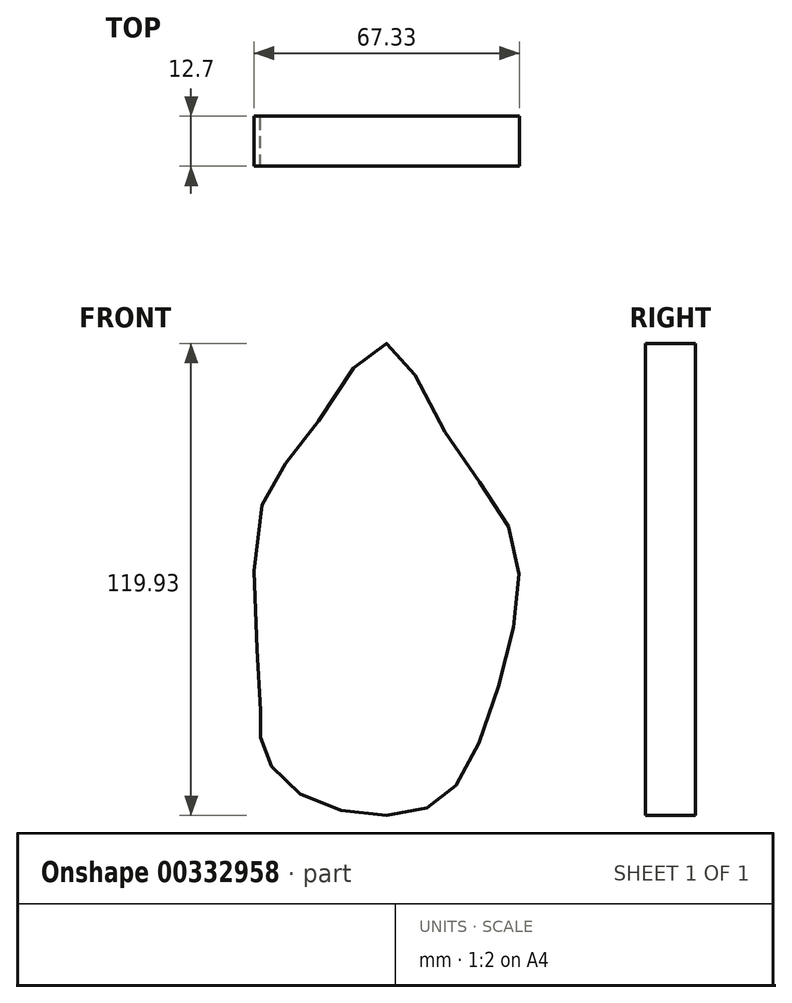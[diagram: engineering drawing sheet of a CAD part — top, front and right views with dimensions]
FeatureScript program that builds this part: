
annotation { "Feature Type Name" : "Feature", "Feature Type Description" : "" }
export const myFeature = defineFeature(function(context is Context, id is Id, definition is map)
    precondition{}
    {
        {
            var Q0;
            Q0=qCreatedBy(makeId("Front.planeOp"),FACE);
            var sketch = newSketch(context, id + "F0", { "sketchPlane" : qUnion([Q0])});
            skFitSpline(sketch, "E0", {"points": [v(-31.37, -29.84) * mm, v(-31.37, -37.25) * mm, v(-26.14, -47.27) * mm, v(-9.58, -55.54) * mm, v(9.58, -55.1) * mm, v(20.47, -45.52) * mm, v(31.8, -13.29) * mm, v(32.67, 14.16) * mm, v(15.25, 41.17) * mm, v(0, 63.39) * mm, v(-18.73, 40.73) * mm, v(-31.8, 19.39) * mm, v(-31.37, -29.84) * mm]});
            skSolve(sketch);
        }
        {
            var Q0;
            Q0=makeQuery(id+"F0.imprint","IMPRINT",FACE,{"disambiguationData":[TD([[makeQuery(id+"F0.imprint","IMPRINT",EDGE,{"derivedFrom":sQuery(id+"F0.wireOp",EDGE,"E0")}),1.0]])]});
            extrude(context, id + "F1", {"entities" : qUnion([Q0]), "depth" : 12.7 * mm});
        }
    });
